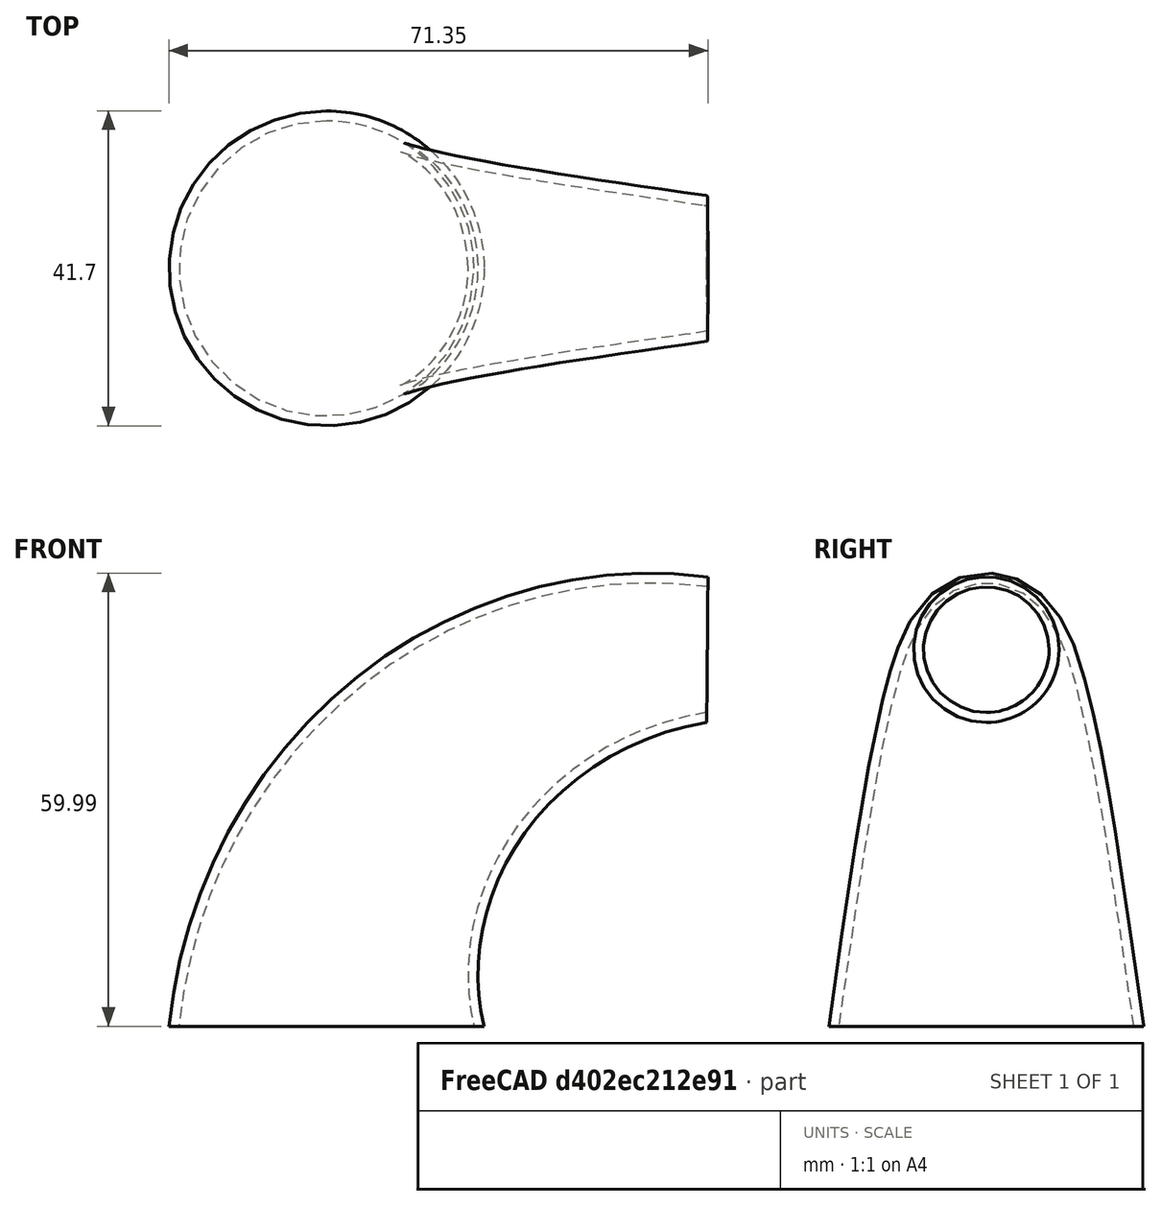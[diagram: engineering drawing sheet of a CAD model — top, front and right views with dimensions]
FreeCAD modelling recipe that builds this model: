
FCSTD DOCUMENT  (FreeCAD 0.21R33771 (Git))
Label: truba
License: All rights reserved
LicenseURL: http://en.wikipedia.org/wiki/All_rights_reserved
objects: Sketcher::SketchObject×3, PartDesign::AdditivePipe×1, PartDesign::Thickness×1, PartDesign::Body×1
note: 8 computed .brp shape members not serialized (recipe doc carries the construction recipe); baked Part::Feature solids carry a one-line shape summary decoded from their .brp

FEATURE [Sketcher::SketchObject] Sketch
  FullyConstrained = false
  MapMode = 5
  Support = -> [XY_Plane]
  sketch-geometry (1):
    g0: Circle CenterX=0 CenterY=0 CenterZ=0 NormalX=0 NormalY=0 NormalZ=1 AngleXU=0 Radius=19.5339
  constraints (1):
    c: Coincident(g0,g-1)
FEATURE [Sketcher::SketchObject] Sketch001
  AttachmentOffset = pos=(0,22,50) rot=(0,0,1;0rad)
  FullyConstrained = false
  MapMode = 5
  Placement = pos=(50,-6.2e-15,22) rot=(0.57735,0.57735,0.57735;2.0944rad)
  Support = -> [YZ_Plane]
  sketch-geometry (1):
    g0: Circle CenterX=0 CenterY=27.8702 CenterZ=0 NormalX=0 NormalY=0 NormalZ=1 AngleXU=0 Radius=8.37957
  constraints (1):
    c: PointOnObject(g0,g-2)
FEATURE [Sketcher::SketchObject] Sketch002
  FullyConstrained = false
  MapMode = 5
  Placement = pos=(0,0,0) rot=(1,0,0;1.5708rad)
  Support = -> [XZ_Plane]
  sketch-geometry (4):
    g0: ArcOfCircle CenterX=49.9934 CenterY=0 CenterZ=0 NormalX=0 NormalY=0 NormalZ=1 AngleXU=0 Radius=49.9934 StartAngle=1.56211 EndAngle=3.13786
    g1: GeomPoint X=50.4276 Y=49.9916 Z=0
    g2: LineSegment StartX=50.4276 StartY=49.9916 StartZ=0 EndX=52.8719 EndY=52.2922 EndZ=0
    g3: LineSegment StartX=0.000348254 StartY=0.186603 StartZ=0 EndX=-4.15514 EndY=-1.5307 EndZ=0
  constraints (5):
    c: PointOnObject(g0,g-1)
    c: PointOnObject(g-1,g0)
    c: Coincident(g2,g1)
    c: Coincident(g0,g3)
    c: Coincident(g0,g2)
FEATURE [PartDesign::AdditivePipe] AdditivePipe
  AuxilleryCurvelinear = true
  AuxillerySpineTangent = false
  Binormal = (0,0,0)
  Mode = 0
  Profile = -> Sketch
  Refine = true
  Sections = -> [Sketch001]
  Spine = -> Sketch002 [Edge1]
  SpineTangent = false
  Transformation = 1
  Transition = 0
FEATURE [PartDesign::Thickness] Thickness
  Base = -> AdditivePipe [Face1,Face3]
  BaseFeature = -> AdditivePipe
  Intersection = false
  Join = 0
  Mode = 0
  Refine = true
  SupportTransform = false
  Value = 1.3
FEATURE [PartDesign::Body] Body
  Group = -> [Sketch,Sketch001,Sketch002,AdditivePipe,Thickness]
  Origin = -> Origin
  Tip = -> Thickness
